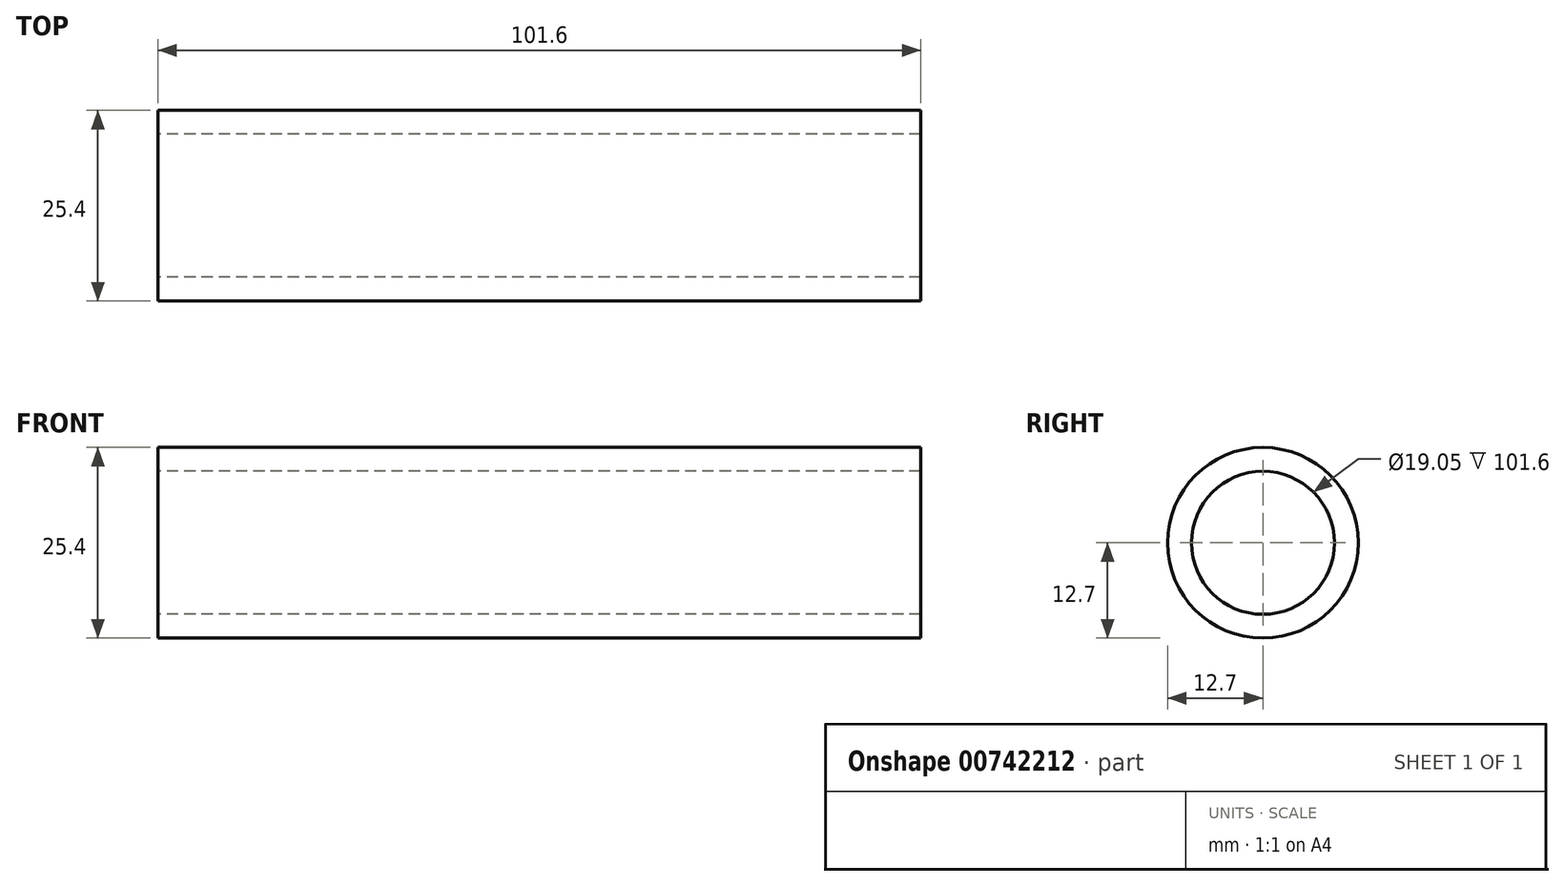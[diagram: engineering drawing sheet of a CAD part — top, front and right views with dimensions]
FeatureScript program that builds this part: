
annotation { "Feature Type Name" : "Feature", "Feature Type Description" : "" }
export const myFeature = defineFeature(function(context is Context, id is Id, definition is map)
    precondition{}
    {
        {
            var Q0;
            Q0=qCreatedBy(makeId("Right.planeOp"),FACE);
            var sketch = newSketch(context, id + "F0", { "sketchPlane" : qUnion([Q0])});
            skCircle(sketch, "E0", {"center": v(0, 0) * mm, "radius": 12.7 * mm});
            skCircle(sketch, "E1", {"center": v(0, 0) * mm, "radius": 9.53 * mm});
            skSolve(sketch);
        }
        {
            var Q0;
            Q0=makeQuery(id+"F0.imprint","IMPRINT",FACE,{"disambiguationData":[TD([[makeQuery(id+"F0.imprint","IMPRINT",EDGE,{"derivedFrom":sQuery(id+"F0.wireOp",EDGE,"E0")}),1.0]])]});
            extrude(context, id + "F1", {"entities" : qUnion([Q0]), "depth" : 101.6 * mm, "offsetDistance" : 25.4 * mm});
        }
    });
